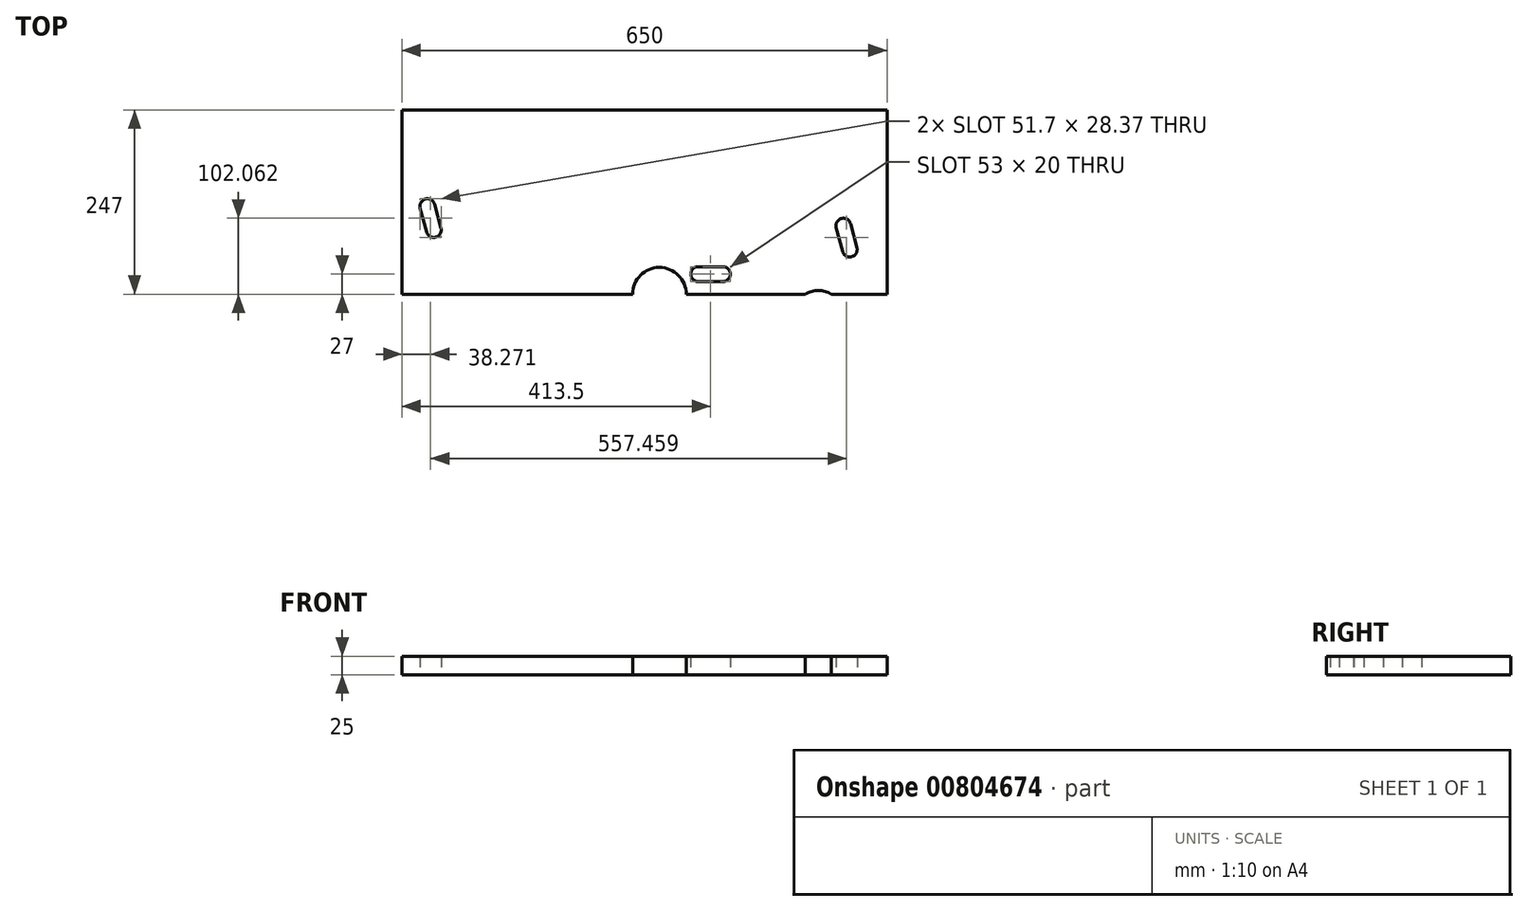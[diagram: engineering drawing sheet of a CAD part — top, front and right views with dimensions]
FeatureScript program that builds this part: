
annotation { "Feature Type Name" : "Feature", "Feature Type Description" : "" }
export const myFeature = defineFeature(function(context is Context, id is Id, definition is map)
    precondition{}
    {
        {
            var Q0;
            Q0=qCreatedBy(makeId("Top.planeOp"),FACE);
            var sketch = newSketch(context, id + "F0", { "sketchPlane" : qUnion([Q0])});
            skLineSegment(sketch, "E0.bottom", {"start": v(-325, 123.5) * mm, "end": v(325, 123.5) * mm});
            skLineSegment(sketch, "E0.top", {"start": v(-325, -123.5) * mm, "end": v(-16, -123.5) * mm});
            skLineSegment(sketch, "E0.left", {"start": v(-325, 123.5) * mm, "end": v(-325, -123.5) * mm});
            skLineSegment(sketch, "E0.right", {"start": v(325, 123.5) * mm, "end": v(325, -123.5) * mm});
            skPoint(sketch, "E1", {"position": v(0, 123.5) * mm});
            skPoint(sketch, "E2", {"position": v(-325, 0) * mm});
            skArc(sketch, "E3", {"start": v(56, -123.5) * mm, "mid": v(20, -87.5) * mm, "end": v(-16, -123.5) * mm});
            skLineSegment(sketch, "E4.trimOffspring", {"start": v(56, -123.5) * mm, "end": v(215.54, -123.5) * mm});
            skArc(sketch, "E5", {"start": v(250.46, -123.5) * mm, "mid": v(233, -118.5) * mm, "end": v(215.54, -123.5) * mm});
            skLineSegment(sketch, "E6.trimOffspring", {"start": v(250.46, -123.5) * mm, "end": v(325, -123.5) * mm});
            skArc(sketch, "E7", {"start": v(105, -106.5) * mm, "mid": v(115, -96.5) * mm, "end": v(105, -86.5) * mm});
            skArc(sketch, "E8.1.0.0", {"start": v(72, -86.5) * mm, "mid": v(62, -96.5) * mm, "end": v(72, -106.5) * mm});
            skLineSegment(sketch, "E8.direction1", {"start": v(105, -96.5) * mm, "end": v(72, -96.5) * mm, "construction": true});
            skLineSegment(sketch, "E9", {"start": v(72, -86.5) * mm, "end": v(105, -86.5) * mm});
            skLineSegment(sketch, "E10", {"start": v(105, -106.5) * mm, "end": v(72, -106.5) * mm});
            skArc(sketch, "E11", {"start": v(276.12, -29.04) * mm, "mid": v(263.87, -21.97) * mm, "end": v(256.8, -34.21) * mm});
            skArc(sketch, "E12.1.0.0", {"start": v(265.34, -66.09) * mm, "mid": v(277.59, -73.16) * mm, "end": v(284.66, -60.91) * mm});
            skLineSegment(sketch, "E12.direction1", {"start": v(266.46, -31.62) * mm, "end": v(275, -63.5) * mm, "construction": true});
            skLineSegment(sketch, "E13", {"start": v(265.34, -66.09) * mm, "end": v(256.8, -34.21) * mm});
            skLineSegment(sketch, "E14", {"start": v(276.12, -29.04) * mm, "end": v(284.66, -60.91) * mm});
            skLineSegment(sketch, "E15.0", {"start": v(276.12, -29.04) * mm, "end": v(256.8, -34.21) * mm, "construction": true});
            skArc(sketch, "E16", {"start": v(-281.34, -2.91) * mm, "mid": v(-293.59, 4.16) * mm, "end": v(-300.66, -8.09) * mm});
            skArc(sketch, "E17.1.0.0", {"start": v(-292.12, -39.96) * mm, "mid": v(-279.87, -47.03) * mm, "end": v(-272.8, -34.79) * mm});
            skLineSegment(sketch, "E17.direction1", {"start": v(-291, -5.5) * mm, "end": v(-282.46, -37.38) * mm, "construction": true});
            skLineSegment(sketch, "E18", {"start": v(-292.12, -39.96) * mm, "end": v(-300.66, -8.09) * mm});
            skLineSegment(sketch, "E19", {"start": v(-281.34, -2.91) * mm, "end": v(-272.8, -34.79) * mm});
            skLineSegment(sketch, "E20.0", {"start": v(-281.34, -2.91) * mm, "end": v(-300.66, -8.09) * mm, "construction": true});
            skSolve(sketch);
        }
        {
            var Q0;
            Q0 = qSketchRegion(id + "F0", true);
            extrude(context, id + "F1", {"entities" : qUnion([Q0]), "depth" : 20 * mm, "offsetDistance" : 25 * mm});
        }
        {
            var Q0;
            Q0 = qSketchRegion(id + "F0", true);
            extrude(context, id + "F2", {"entities" : qUnion([Q0]), "operationType" : NewBodyOperationType.ADD, "depth" : 25 * mm, "offsetDistance" : 25 * mm});
        }
    });
